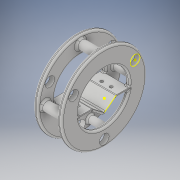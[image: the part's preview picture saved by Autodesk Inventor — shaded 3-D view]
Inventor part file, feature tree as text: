
AUTODESK INVENTOR PART (.ipt)
format: ipt  version: 2019 (Build 230136000, 136)  size: 696,320 bytes
history: native  units: in
note: dims shown in document units (in); Inventor stores cm internally (conversion verified against a paired STEP export)
features: fillet x12, sketch x9, extrude x7, mirror x2, projected_geometry x2, plane x1, pattern_circular x1
ambient origin geometry x8: Origin, YZ Plane, XZ Plane, XY Plane, X Axis, Y Axis, Z Axis, Center Point
bodies: Solid1 (feature_tree)
feature tree (34):
  extrude  "Extrusion1"  Depth=0.7087in
  extrude  "Extrusion2"  Depth=0.5118in
  mirror  "Mirror1"
  extrude  "Extrusion3"  Depth=0.3603in
  plane  "Work Plane1"
  extrude  "Extrusion4"  Depth=0.1181in
  extrude  "Extrusion5"  Depth=1.1811in TaperAngle=0.0deg
  pattern_circular  "Circular Pattern1"  Count=3  [1 undecoded]
  extrude  "Extrusion6"  Depth=0.1969in TaperAngle=0.0deg
  extrude  "Extrusion7"  Depth=0.4016in
  mirror  "Mirror2"
  sketch  "Sketch12"  dims[d51=0.0787in]
  sketch  "Sketch14"  dims[d52=90.0deg d53=0.122in d55=0.0787in d56=0.0787in d57=0.0591in d58=0.0787in d59=0.0787in d60=0.0787in d61=0.0787in d62=0.0787in d63=0.0787in d64=0.1969in d66=0.0591in d68=0.0591in d69=0.0591in d70=0.7087in]
  fillet  "Fillet2"  Radius=1.9685in
  fillet  "Fillet3"  Radius=1.1811in
  fillet  "Fillet4"  Radius=2.9528in
  fillet  "Fillet5"  Radius=0.3543in
  fillet  "Fillet6"  Radius=0.2756in
  fillet  "Fillet7"  Radius=0.2756in
  fillet  "Fillet8"  Radius=0.3543in
  fillet  "Fillet9"  Radius=0.3543in
  fillet  "Fillet10"  Radius=1.1811in
  fillet  "Fillet12"  Radius=0.122in
  fillet  "Fillet14"  Radius=0.1969in
  fillet  "Fillet15"  Radius=0.7087in
  sketch  "Sketch2"  dims[d4=3.5433in d5=0.7087in]
  sketch  "Sketch4"  dims[d6=0.1969in d7=0.0in d16=0.5118in]
  sketch  "Sketch5"  dims[d17=0.5118in d18=0.3603in]
  projected_geometry  "Projected Loop1"
  sketch  "Sketch6"  dims[d20=0.1181in d21=0.1181in]
  projected_geometry  "Projected Loop2"
  sketch  "Sketch9"  dims[d22=180.0deg d23=1.1811in d24=0.0in d25=1.1811in d26=0.0in]
  sketch  "Sketch10"  dims[d27=-1.1811in d28=0.1969in d29=0.0in]
  sketch  "Sketch11"  dims[d32=2.9528in d33=0.4016in d34=1.9685in d35=0.0in d36=1.1811in d37=360.0deg d39=2.9528in d40=0.3543in d41=0.2756in d42=0.2756in d43=0.3543in d44=0.3543in d45=1.1811in d46=0.0in d47=0.122in d48=0.1969in d49=0.0in d50=0.7087in]
note: 1 required parameter value undecoded (feature->parameter linkage not recoverable at this tier; creation-order binding heuristic only, values carry confidence <= 0.55)
